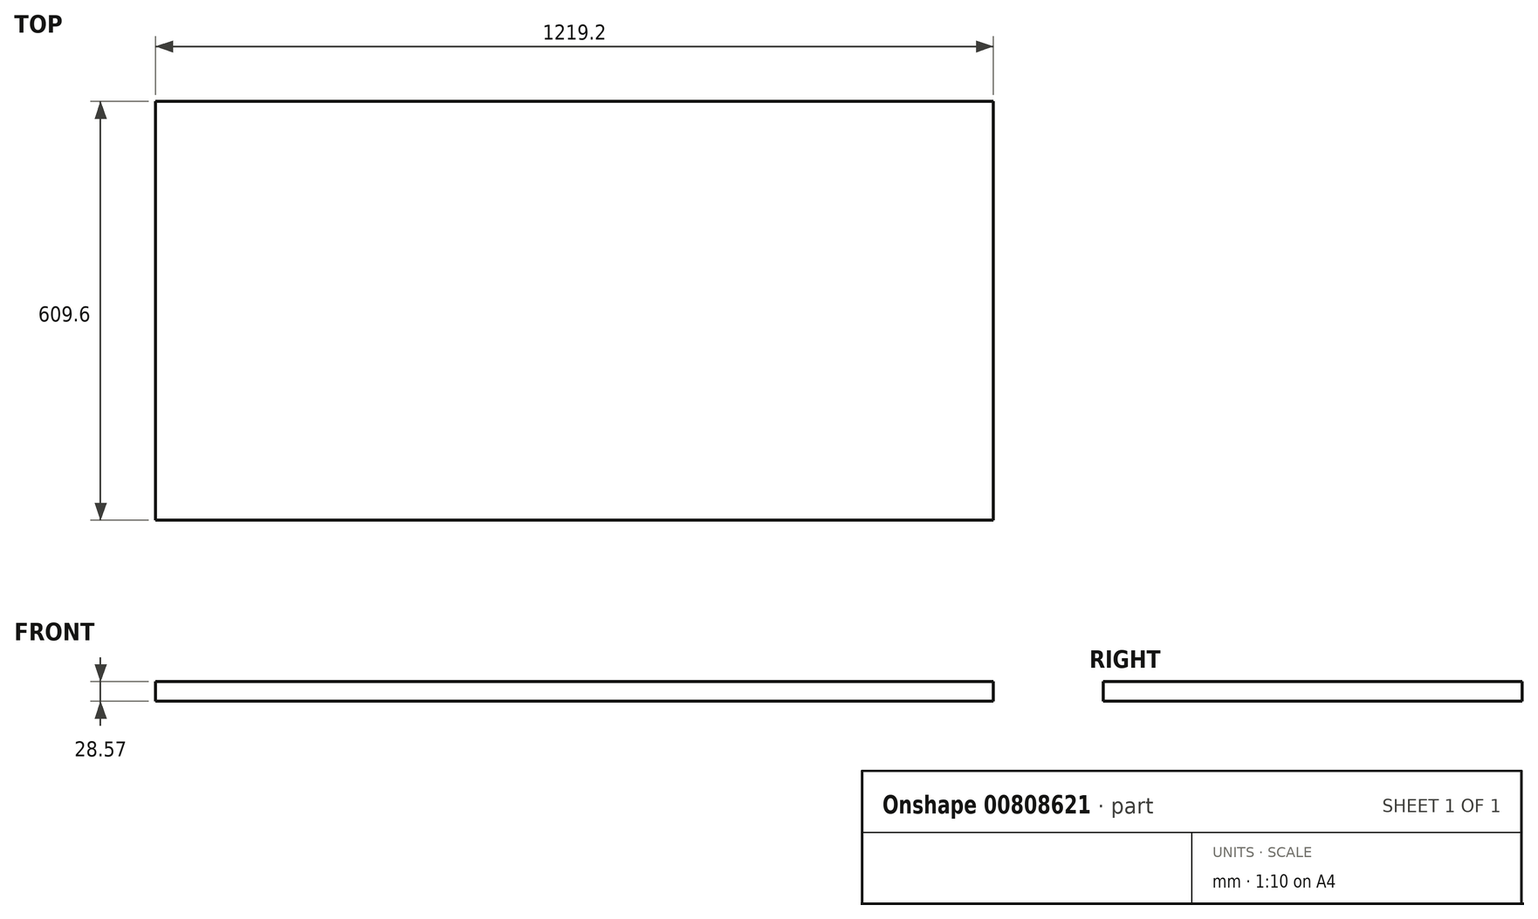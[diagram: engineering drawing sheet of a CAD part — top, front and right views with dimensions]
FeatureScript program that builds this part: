
annotation { "Feature Type Name" : "Feature", "Feature Type Description" : "" }
export const myFeature = defineFeature(function(context is Context, id is Id, definition is map)
    precondition{}
    {
        {
            var Q0;
            Q0=qCreatedBy(makeId("Top.planeOp"),FACE);
            var sketch = newSketch(context, id + "F0", { "sketchPlane" : qUnion([Q0])});
            skLineSegment(sketch, "E0.bottom", {"start": v(-609.6, 304.8) * mm, "end": v(609.6, 304.8) * mm});
            skLineSegment(sketch, "E0.top", {"start": v(-609.6, -304.8) * mm, "end": v(609.6, -304.8) * mm});
            skLineSegment(sketch, "E0.left", {"start": v(-609.6, 304.8) * mm, "end": v(-609.6, -304.8) * mm});
            skLineSegment(sketch, "E0.right", {"start": v(609.6, 304.8) * mm, "end": v(609.6, -304.8) * mm});
            skPoint(sketch, "E0.middle", {"position": v(0, 0) * mm});
            skSolve(sketch);
        }
        {
            var Q0;
            Q0=makeQuery(id+"F0.imprint","IMPRINT",FACE,{"disambiguationData":[TD([[makeQuery(id+"F0.imprint","IMPRINT",EDGE,{"derivedFrom":sQuery(id+"F0.wireOp",EDGE,"E0.bottom")}),-1.0]])]});
            extrude(context, id + "F1", {"entities" : qUnion([Q0]), "depth" : 28.57 * mm, "offsetDistance" : 25.4 * mm});
        }
    });
